FCSTD DOCUMENT  (FreeCAD 0.20R29603 (Git))
Label: outline
License: All rights reserved
LicenseURL: http://en.wikipedia.org/wiki/All_rights_reserved
objects: App::DocumentObjectGroup×2, Sketcher::SketchObject×1, PartDesign::CoordinateSystem×1, App::FeaturePython×1, App::Part×1
note: 2 computed .brp shape members not serialized (recipe doc carries the construction recipe); baked Part::Feature solids carry a one-line shape summary decoded from their .brp

FEATURE [Sketcher::SketchObject] Sketch
  FullyConstrained = true
  sketch-geometry (12):
    g0: ArcOfCircle CenterX=-0.0237158 CenterY=8.61554 CenterZ=0 NormalX=0 NormalY=0 NormalZ=1 AngleXU=0 Radius=8 StartAngle=3.21861 EndAngle=3.65304
    g1: LineSegment StartX=7 StartY=8 StartZ=0 EndX=7 EndY=36.2 EndZ=0
    g2: LineSegment StartX=-8 StartY=8 StartZ=0 EndX=-8 EndY=36.2 EndZ=0
    g3: ArcOfCircle CenterX=-9.10829 CenterY=37.4759 CenterZ=0 NormalX=0 NormalY=0 NormalZ=1 AngleXU=0 Radius=1.69 StartAngle=5.42762 EndAngle=6.08916
    g4: ArcOfCircle CenterX=8.10829 CenterY=37.4759 CenterZ=0 NormalX=0 NormalY=0 NormalZ=1 AngleXU=0 Radius=1.69 StartAngle=3.33562 EndAngle=3.99716
    g5: ArcOfCircle CenterX=-0.999754 CenterY=7.93728 CenterZ=0 NormalX=0 NormalY=0 NormalZ=1 AngleXU=0 Radius=8 StartAngle=4.83769 EndAngle=6.29102
    g6: ArcOfCircle CenterX=-5.87989 CenterY=-1.19452 CenterZ=0 NormalX=0 NormalY=0 NormalZ=1 AngleXU=0 Radius=6 StartAngle=0.200426 EndAngle=1.75858
    g7: LineSegment StartX=-7.45 StartY=37.15 StartZ=0 EndX=6.45 EndY=37.15 EndZ=0
    g8: LineSegment StartX=-7.45 StartY=37.15 StartZ=0 EndX=-8 EndY=37.15 EndZ=0
    g9: LineSegment StartX=-8 StartY=36.2 StartZ=0 EndX=-8 EndY=37.15 EndZ=0
    g10: LineSegment StartX=6.45 StartY=37.15 StartZ=0 EndX=7 EndY=37.15 EndZ=0
    g11: LineSegment StartX=7 StartY=36.2 StartZ=0 EndX=7 EndY=37.15 EndZ=0
  constraints (38):
    c: Coincident(g1,g5)
    c: Coincident(g5,g6)
    c: Coincident(g0,g6)
    c: Coincident(g0,g2)
    c: Coincident(g2,g3)
    c: Coincident(g1,g4)
    c: Coincident(g3,g7)
    c: Coincident(g4,g7)
    c: DistanceX(g7,g7) = 13.9
    c: Radius(g4) = 1.69
    c: Radius(g3) = 1.69
    c: Equal(g1,g2)
    c: DistanceY(g1,g1) = 28.2
    c: DistanceX(g0,g1) = 15
    c: Radius(g5) = 8
    c: Radius(g0) = 8
    c: Radius(g6) = 6
    c: DistanceY(g5,g1) = 8
    c: DistanceX(g5,g1) = 7
    c: DistanceY(g0,g0) = 3.3
    c: Vertical(g2)
    c: Vertical(g1)
    c: Horizontal(g7)
    c: DistanceY(g2,g3) = 0.95
    c: DistanceY(g1,g4) = 0.95
    c: DistanceX(g0,g5) = 7
    c: Coincident(g5,g-1)
    c: Coincident(g1,g11)
    c: Coincident(g10,g11)
    c: Coincident(g4,g10)
    c: Horizontal(g10)
    c: Vertical(g11)
    c: Coincident(g2,g9)
    c: Coincident(g8,g9)
    c: Coincident(g3,g8)
    c: Horizontal(g8)
    c: Vertical(g9)
    c: Equal(g8,g10)
FEATURE [App::DocumentObjectGroup] Parts
FEATURE [PartDesign::CoordinateSystem] LCS_Origin
  AttacherType = Attacher::AttachEngine3D
  MapMode = 2
  Support = -> [X_Axis]
FEATURE [App::DocumentObjectGroup] Constraints
FEATURE [App::FeaturePython] Variables  # WARN: FeaturePython — macro-defined, semantics opaque (R4)
FEATURE [App::Part] Model
  Configuration = 0
  Group = -> [LCS_Origin,Constraints,Variables,Sketch]
  Origin = -> Origin
  Type = Assembly4 Model
